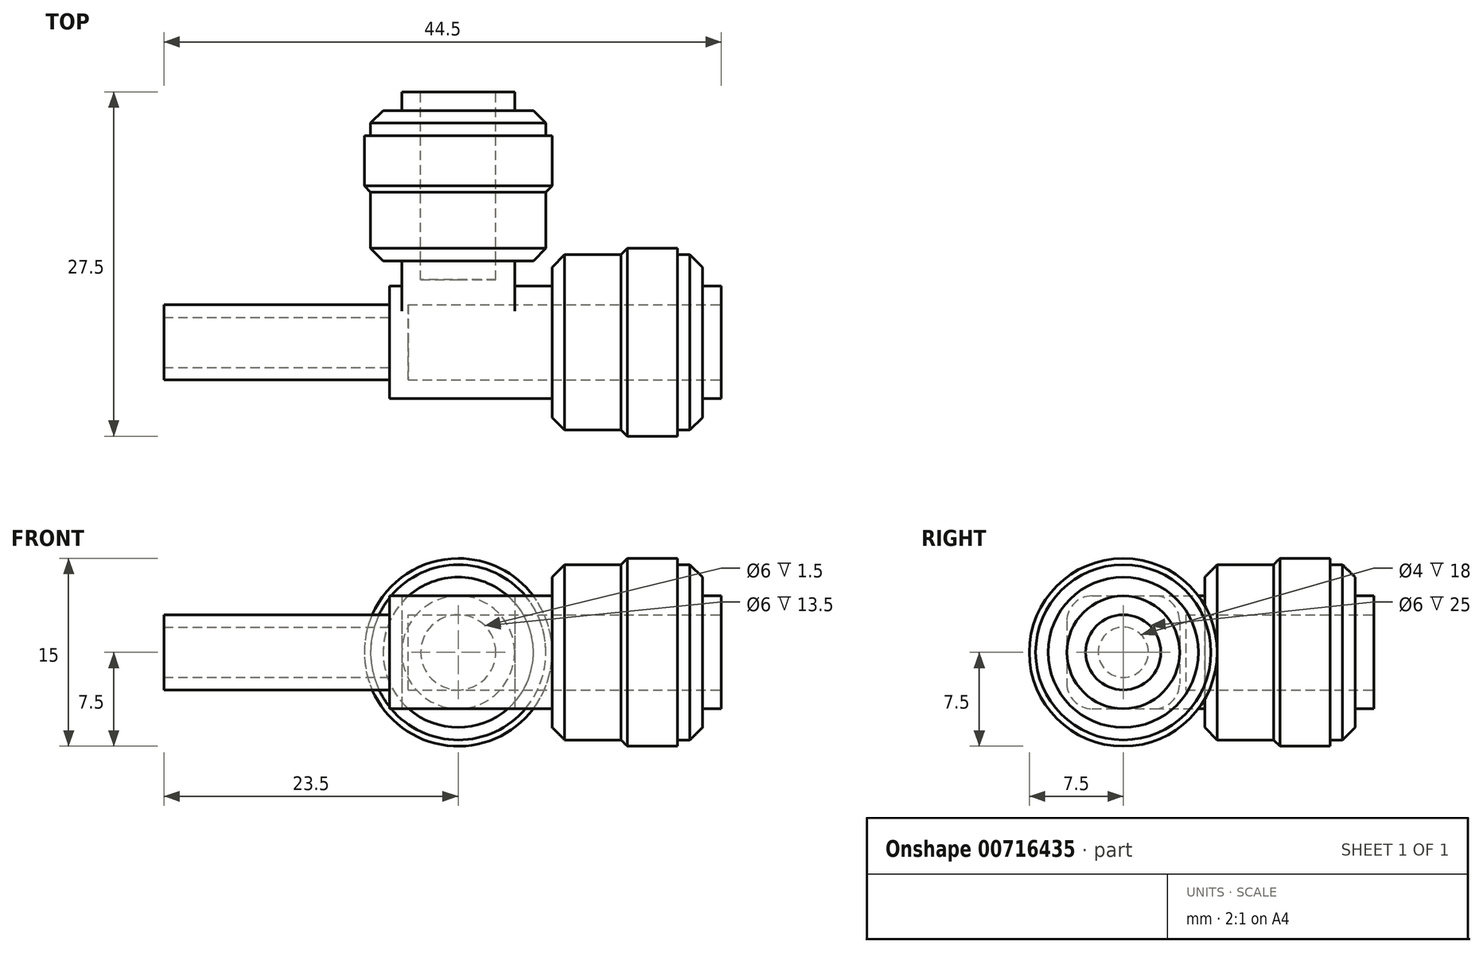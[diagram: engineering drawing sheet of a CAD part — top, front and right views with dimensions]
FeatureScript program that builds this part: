
annotation { "Feature Type Name" : "Feature", "Feature Type Description" : "" }
export const myFeature = defineFeature(function(context is Context, id is Id, definition is map)
    precondition{}
    {
        {
            var Q0;
            Q0=qCreatedBy(makeId("Top.planeOp"),FACE);
            var sketch = newSketch(context, id + "F0", { "sketchPlane" : qUnion([Q0])});
            skLineSegment(sketch, "E0.bottom", {"start": v(3, -4.5) * mm, "end": v(-10, -4.5) * mm});
            skLineSegment(sketch, "E0.top", {"start": v(3, 4.5) * mm, "end": v(0, 4.5) * mm});
            skLineSegment(sketch, "E0.right", {"start": v(-10, -4.5) * mm, "end": v(-10, 4.5) * mm});
            skPoint(sketch, "E0.middle", {"position": v(0, 0) * mm});
            skLineSegment(sketch, "E1.trimOffspring", {"start": v(-9, 4.5) * mm, "end": v(-10, 4.5) * mm});
            skLineSegment(sketch, "E2.top", {"start": v(-9, 6.5) * mm, "end": v(0, 6.5) * mm});
            skLineSegment(sketch, "E2.left", {"start": v(-9, 4.5) * mm, "end": v(-9, 6.5) * mm});
            skLineSegment(sketch, "E2.right", {"start": v(0, 4.5) * mm, "end": v(0, 6.5) * mm});
            skPoint(sketch, "E3.orphan", {"position": v(0, 4.5) * mm});
            skLineSegment(sketch, "E4", {"start": v(3, 4.5) * mm, "end": v(3, -4.5) * mm});
            skPoint(sketch, "E5.orphan", {"position": v(10, 4.5) * mm});
            skPoint(sketch, "E6.orphan", {"position": v(10, -4.5) * mm});
            skSolve(sketch);
        }
        {
            var Q0;
            Q0 = qSketchRegion(id + "F0", true);
            extrude(context, id + "F1", {"entities" : qUnion([Q0]), "depth" : 9 * mm, "offsetDistance" : 25 * mm});
        }
        {
            var Q0;
            Q0=makeQuery(id+"F1.opExtrude","CAP_EDGE",EDGE,{"disambiguationData":[OSD([sQuery(id+"F0.wireOp",EDGE,"E0.bottom")])],"isStart":false});
            var Q1;
            Q1=makeQuery(id+"F1.opExtrude","CAP_EDGE",EDGE,{"disambiguationData":[OSD([sQuery(id+"F0.wireOp",EDGE,"E0.bottom")])],"isStart":true});
            var Q2;
            Q2=makeQuery(id+"F1.opExtrude","CAP_EDGE",EDGE,{"disambiguationData":[OSD([sQuery(id+"F0.wireOp",EDGE,"E0.top")])],"isStart":true});
            var Q3;
            Q3=makeQuery(id+"F1.opExtrude","CAP_EDGE",EDGE,{"disambiguationData":[OSD([sQuery(id+"F0.wireOp",EDGE,"8505e65d-c6b5-42ff-a061-037604a2aff11.MirrorCS")])],"isStart":true});
            var Q4;
            Q4=makeQuery(id+"F1.opExtrude","CAP_EDGE",EDGE,{"disambiguationData":[OSD([sQuery(id+"F0.wireOp",EDGE,"E0.top")])],"isStart":false});
            var Q5;
            Q5=makeQuery(id+"F1.opExtrude","CAP_EDGE",EDGE,{"disambiguationData":[OSD([sQuery(id+"F0.wireOp",EDGE,"8505e65d-c6b5-42ff-a061-037604a2aff11.MirrorCS")])],"isStart":false});
            var Q6;
            Q6=makeQuery(id+"F1.opExtrude","CAP_EDGE",EDGE,{"disambiguationData":[OSD([sQuery(id+"F0.wireOp",EDGE,"r2ULZHA1-oAAN-rar3-eHOP-QA2KXA1UHW2E")])],"isStart":false});
            var Q7;
            Q7=makeQuery(id+"F1.opExtrude","CAP_EDGE",EDGE,{"disambiguationData":[OSD([sQuery(id+"F0.wireOp",EDGE,"E1.trimOffspring")])],"isStart":false});
            var Q8;
            Q8=makeQuery(id+"F1.opExtrude","CAP_EDGE",EDGE,{"disambiguationData":[OSD([sQuery(id+"F0.wireOp",EDGE,"E1.trimOffspring")])],"isStart":true});
            var Q9;
            Q9=makeQuery(id+"F1.opExtrude","CAP_EDGE",EDGE,{"disambiguationData":[OSD([sQuery(id+"F0.wireOp",EDGE,"r2ULZHA1-oAAN-rar3-eHOP-QA2KXA1UHW2E")])],"isStart":true});
            fillet(context, id + "F2", {"entities" : qUnion([Q0, Q1, Q2, Q3, Q4, Q5, Q6, Q7, Q8, Q9]), "radius" : 2 * mm, "tangentPropagation" : true, "allowEdgeOverflow" : false});
        }
        {
            var Q0;
            Q0=makeQuery(id+"F1.opExtrude","SWEPT_FACE",FACE,{"disambiguationData":[OSD([sQuery(id+"F0.wireOp",EDGE,"E0.right")])]});
            var sketch = newSketch(context, id + "F3", { "sketchPlane" : qUnion([Q0])});
            skPoint(sketch, "E7.centerSnap0", {"position": v(4.5, 4.5) * mm});
            skCircle(sketch, "E8", {"center": v(0, 4.5) * mm, "radius": 3 * mm});
            skCircle(sketch, "E9", {"center": v(0, 4.5) * mm, "radius": 2 * mm});
            skSolve(sketch);
        }
        {
            var Q0;
            Q0 = qSketchRegion(id + "F3", true);
            extrude(context, id + "F4", {"entities" : qUnion([Q0]), "operationType" : NewBodyOperationType.ADD, "depth" : 18 * mm, "offsetDistance" : 25 * mm});
        }
        {
            var Q0;
            Q0=makeQuery(id+"F1.opExtrude","SWEPT_FACE",FACE,{"disambiguationData":[OSD([sQuery(id+"F0.wireOp",EDGE,"E2.top")])]});
            var sketch = newSketch(context, id + "F5", { "sketchPlane" : qUnion([Q0])});
            skCircle(sketch, "E10", {"center": v(4.5, 4.5) * mm, "radius": 7 * mm});
            skPoint(sketch, "E10.centerSnap0", {"position": v(4.5, 0) * mm});
            skPoint(sketch, "E10.centerSnap1", {"position": v(9, 4.5) * mm});
            skSolve(sketch);
        }
        {
            var Q0;
            Q0 = qSketchRegion(id + "F5", true);
            extrude(context, id + "F6", {"entities" : qUnion([Q0]), "depth" : 5 * mm, "offsetDistance" : 25 * mm});
        }
        {
            var Q0;
            Q0=makeQuery(id+"F6.opExtrude","CAP_EDGE",EDGE,{"disambiguationData":[OSD([sQuery(id+"F5.wireOp",EDGE,"E10")])],"isStart":true});
            chamfer(context, id + "F7", {"entities" : qUnion([Q0]), "width" : 1 * mm, "tangentPropagation" : true});
        }
        {
            var Q0;
            Q0=makeQuery(id+"F6.opExtrude","CAP_FACE",FACE,{"disambiguationData":[OSD([sQuery(id+"F5.wireOp",EDGE,"E10")])],"isStart":false});
            var sketch = newSketch(context, id + "F8", { "sketchPlane" : qUnion([Q0])});
            skCircle(sketch, "E11", {"center": v(4.5, 4.5) * mm, "radius": 7.5 * mm});
            skSolve(sketch);
        }
        {
            var Q0;
            Q0 = qSketchRegion(id + "F8", true);
            extrude(context, id + "F9", {"entities" : qUnion([Q0]), "operationType" : NewBodyOperationType.ADD, "depth" : 5 * mm, "offsetDistance" : 25 * mm});
        }
        {
            var Q0;
            Q0=makeQuery(id+"F9.opExtrude","CAP_EDGE",EDGE,{"disambiguationData":[OSD([sQuery(id+"F8.wireOp",EDGE,"E11")])],"isStart":true});
            chamfer(context, id + "F10", {"entities" : qUnion([Q0]), "width" : 1 * mm, "tangentPropagation" : true});
        }
        {
            var Q0;
            Q0=makeQuery(id+"F9.opExtrude","CAP_FACE",FACE,{"disambiguationData":[OSD([sQuery(id+"F8.wireOp",EDGE,"E11")])],"isStart":false});
            var sketch = newSketch(context, id + "F11", { "sketchPlane" : qUnion([Q0])});
            skCircle(sketch, "E12", {"center": v(4.5, 4.5) * mm, "radius": 7 * mm});
            skSolve(sketch);
        }
        {
            var Q0;
            Q0 = qSketchRegion(id + "F11", true);
            extrude(context, id + "F12", {"entities" : qUnion([Q0]), "operationType" : NewBodyOperationType.ADD, "depth" : 2 * mm, "offsetDistance" : 25 * mm});
        }
        {
            var Q0;
            Q0=makeQuery(id+"F12.opExtrude","CAP_EDGE",EDGE,{"disambiguationData":[OSD([sQuery(id+"F11.wireOp",EDGE,"E12")])],"isStart":false});
            chamfer(context, id + "F13", {"entities" : qUnion([Q0]), "width" : 1 * mm, "tangentPropagation" : true});
        }
        {
            var Q0;
            Q0=makeQuery(id+"F12.opExtrude","CAP_FACE",FACE,{"disambiguationData":[OSD([sQuery(id+"F11.wireOp",EDGE,"E12")])],"isStart":false});
            var sketch = newSketch(context, id + "F14", { "sketchPlane" : qUnion([Q0])});
            skCircle(sketch, "E13", {"center": v(4.5, 4.5) * mm, "radius": 4.5 * mm});
            skSolve(sketch);
        }
        {
            var Q0;
            Q0 = qSketchRegion(id + "F14", true);
            extrude(context, id + "F15", {"entities" : qUnion([Q0]), "operationType" : NewBodyOperationType.ADD, "depth" : 1.5 * mm, "offsetDistance" : 25 * mm});
        }
        {
            var Q0;
            Q0=makeQuery(id+"F15.opExtrude","CAP_FACE",FACE,{"disambiguationData":[OSD([sQuery(id+"F14.wireOp",EDGE,"E13")])],"isStart":false});
            var sketch = newSketch(context, id + "F16", { "sketchPlane" : qUnion([Q0])});
            skCircle(sketch, "E14", {"center": v(4.5, 4.5) * mm, "radius": 3 * mm});
            skSolve(sketch);
        }
        {
            var Q0;
            Q0 = qSketchRegion(id + "F16", true);
            extrude(context, id + "F17", {"entities" : qUnion([Q0]), "operationType" : NewBodyOperationType.REMOVE, "oppositeDirection" : true, "depth" : 15 * mm, "offsetDistance" : 25 * mm});
        }
        {
            var Q0;
            Q0=makeQuery(id+"F1.opExtrude","SWEPT_FACE",FACE,{"disambiguationData":[OSD([sQuery(id+"F0.wireOp",EDGE,"E4")])]});
            var sketch = newSketch(context, id + "F18", { "sketchPlane" : qUnion([Q0])});
            skCircle(sketch, "E15", {"center": v(0, 4.5) * mm, "radius": 7 * mm});
            skPoint(sketch, "E15.centerSnap0", {"position": v(-4.5, 4.5) * mm});
            skSolve(sketch);
        }
        {
            var Q0;
            Q0 = qSketchRegion(id + "F18", true);
            extrude(context, id + "F19", {"entities" : qUnion([Q0]), "operationType" : NewBodyOperationType.ADD, "depth" : 5 * mm, "offsetDistance" : 25 * mm});
        }
        {
            var Q0;
            Q0=makeQuery(id+"F19.opExtrude","CAP_FACE",FACE,{"disambiguationData":[OSD([sQuery(id+"F18.wireOp",EDGE,"E15")])],"isStart":false});
            var sketch = newSketch(context, id + "F20", { "sketchPlane" : qUnion([Q0])});
            skCircle(sketch, "E16", {"center": v(0, 4.5) * mm, "radius": 7.5 * mm});
            skSolve(sketch);
        }
        {
            var Q0;
            Q0 = qSketchRegion(id + "F20", true);
            extrude(context, id + "F21", {"entities" : qUnion([Q0]), "operationType" : NewBodyOperationType.ADD, "depth" : 5 * mm, "offsetDistance" : 25 * mm});
        }
        {
            var Q0;
            Q0=makeQuery(id+"F21.opExtrude","CAP_FACE",FACE,{"disambiguationData":[OSD([sQuery(id+"F20.wireOp",EDGE,"E16")])],"isStart":false});
            var sketch = newSketch(context, id + "F22", { "sketchPlane" : qUnion([Q0])});
            skCircle(sketch, "E17", {"center": v(0, 4.5) * mm, "radius": 7 * mm});
            skSolve(sketch);
        }
        {
            var Q0;
            Q0 = qSketchRegion(id + "F22", true);
            extrude(context, id + "F23", {"entities" : qUnion([Q0]), "operationType" : NewBodyOperationType.ADD, "depth" : 2 * mm, "offsetDistance" : 25 * mm});
        }
        {
            var Q0;
            Q0=makeQuery(id+"F23.opExtrude","CAP_FACE",FACE,{"disambiguationData":[OSD([sQuery(id+"F22.wireOp",EDGE,"E17")])],"isStart":false});
            var sketch = newSketch(context, id + "F24", { "sketchPlane" : qUnion([Q0])});
            skCircle(sketch, "E18", {"center": v(0, 4.5) * mm, "radius": 4.5 * mm});
            skSolve(sketch);
        }
        {
            var Q0;
            Q0 = qSketchRegion(id + "F24", true);
            extrude(context, id + "F25", {"entities" : qUnion([Q0]), "operationType" : NewBodyOperationType.ADD, "depth" : 1.5 * mm, "offsetDistance" : 25 * mm});
        }
        {
            var Q0;
            Q0=makeQuery(id+"F25.opExtrude","CAP_FACE",FACE,{"disambiguationData":[OSD([sQuery(id+"F24.wireOp",EDGE,"E18")])],"isStart":false});
            var sketch = newSketch(context, id + "F26", { "sketchPlane" : qUnion([Q0])});
            skCircle(sketch, "E19", {"center": v(0, 4.5) * mm, "radius": 3 * mm});
            skSolve(sketch);
        }
        {
            var Q0;
            Q0 = qSketchRegion(id + "F26", true);
            extrude(context, id + "F27", {"entities" : qUnion([Q0]), "operationType" : NewBodyOperationType.REMOVE, "oppositeDirection" : true, "depth" : 25 * mm, "offsetDistance" : 25 * mm});
        }
        {
            var Q0;
            Q0=makeQuery(id+"F19.opExtrude","CAP_EDGE",EDGE,{"disambiguationData":[OSD([sQuery(id+"F18.wireOp",EDGE,"E15")])],"isStart":true});
            var Q1;
            Q1=makeQuery(id+"F21.opExtrude","CAP_EDGE",EDGE,{"disambiguationData":[OSD([sQuery(id+"F20.wireOp",EDGE,"E16")])],"isStart":true});
            var Q2;
            Q2=makeQuery(id+"F23.opExtrude","CAP_EDGE",EDGE,{"disambiguationData":[OSD([sQuery(id+"F22.wireOp",EDGE,"E17")])],"isStart":false});
            chamfer(context, id + "F28", {"entities" : qUnion([Q0, Q1, Q2]), "width" : 1 * mm, "tangentPropagation" : true});
        }
    });
